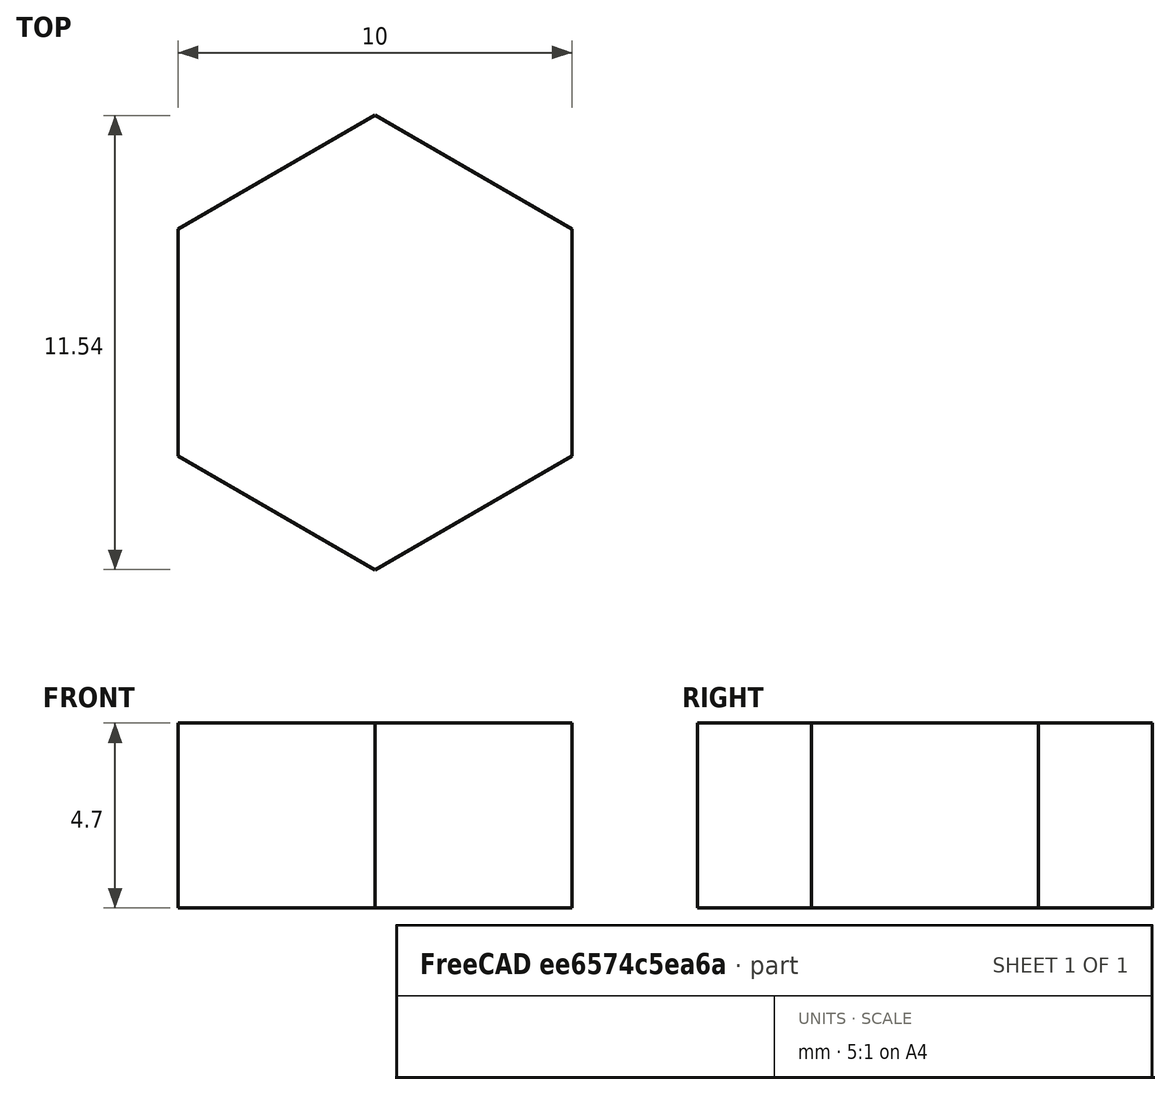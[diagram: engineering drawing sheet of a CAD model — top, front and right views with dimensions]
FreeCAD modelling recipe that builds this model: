
FCSTD DOCUMENT  (FreeCAD 0.16R6700 (Git))
Label: Aula08 - Porca - AUX
License: FreeArt
LicenseURL: http://artlibre.org/licence/lal
objects: Sketcher::SketchObject×2, PartDesign::Pad×1
note: 4 computed .brp shape members not serialized (recipe doc carries the construction recipe); baked Part::Feature solids carry a one-line shape summary decoded from their .brp

FEATURE [Sketcher::SketchObject] Sketch
  sketch-geometry (7):
    g0: LineSegment StartX=5 StartY=2.88675 StartZ=0 EndX=0 EndY=5.7735 EndZ=0
    g1: LineSegment StartX=0 StartY=5.7735 StartZ=0 EndX=-5 EndY=2.88675 EndZ=0
    g2: LineSegment StartX=-5 StartY=2.88675 StartZ=0 EndX=-5 EndY=-2.88675 EndZ=0
    g3: LineSegment StartX=-5 StartY=-2.88675 StartZ=0 EndX=-1e-12 EndY=-5.7735 EndZ=0
    g4: LineSegment StartX=-1e-12 StartY=-5.7735 StartZ=0 EndX=5 EndY=-2.88675 EndZ=0
    g5: LineSegment StartX=5 StartY=-2.88675 StartZ=0 EndX=5 EndY=2.88675 EndZ=0
    g6: Circle [constr] CenterX=0 CenterY=0 CenterZ=0 NormalX=0 NormalY=0 NormalZ=1 Radius=5.7735
  constraints (16):
    c: Coincident(g0,g1)
    c: Coincident(g1,g2)
    c: Coincident(g2,g3)
    c: Coincident(g3,g4)
    c: Coincident(g4,g5)
    c: Coincident(g5,g0)
    c: Equal(g0, g1-g5) x5
    c: PointOnObject(g0,g6)
    c: PointOnObject(g1,g6)
    c: PointOnObject(g2,g6)
    c: PointOnObject(g3,g6)
    c: PointOnObject(g4,g6)
    c: PointOnObject(g5,g6)
    c: Coincident(g6,g-1)
    c: PointOnObject(g0,g-2)
    c: DistanceX(g1,g0) = 10
FEATURE [PartDesign::Pad] Pad
  Length = 4.7
  Length2 = 100
  Sketch = -> Sketch
  Type = 0
FEATURE [Sketcher::SketchObject] Sketch001
  Placement = pos=(0,0,0) rot=(-1,0,0;4.71239rad)
  sketch-geometry (22):
    g0: LineSegment StartX=3 StartY=0 StartZ=0 EndX=1.33699 EndY=0.960141 EndZ=0
    g1: LineSegment StartX=1.33699 StartY=0.960141 StartZ=0 EndX=1.33699 EndY=1.13159 EndZ=0
    g2: LineSegment StartX=1.33699 StartY=1.13159 StartZ=0 EndX=3 EndY=2.09173 EndZ=0
    g3: LineSegment StartX=3 StartY=2.09173 StartZ=0 EndX=1.33699 EndY=3.05187 EndZ=0
    g4: LineSegment StartX=1.33699 StartY=3.05187 StartZ=0 EndX=1.33699 EndY=3.47215 EndZ=0
    g5: LineSegment StartX=1.33699 StartY=3.47215 StartZ=0 EndX=3 EndY=4.43229 EndZ=0
    g6: LineSegment StartX=3 StartY=4.43229 StartZ=0 EndX=1.33699 EndY=5.39243 EndZ=0
    g7: LineSegment StartX=1.33699 StartY=5.39243 StartZ=0 EndX=1.33699 EndY=5.81271 EndZ=0
    g8: LineSegment StartX=1.33699 StartY=5.81271 StartZ=0 EndX=3 EndY=6.77285 EndZ=0
    g9: LineSegment StartX=3 StartY=6.77285 StartZ=0 EndX=1.33699 EndY=7.733 EndZ=0
    g10: LineSegment StartX=1.33699 StartY=7.733 StartZ=0 EndX=1.33699 EndY=7.31271 EndZ=0
    g11: LineSegment StartX=1.33699 StartY=7.31271 StartZ=0 EndX=3 EndY=8.27285 EndZ=0
    g12: LineSegment StartX=3 StartY=8.27285 StartZ=0 EndX=1.33699 EndY=9.233 EndZ=0
    g13: LineSegment StartX=1.33699 StartY=9.233 StartZ=0 EndX=1.33699 EndY=9.40444 EndZ=0
    g14: LineSegment StartX=1.33699 StartY=9.40444 StartZ=0 EndX=3 EndY=10.3646 EndZ=0
    g15: LineSegment StartX=3 StartY=10.3646 StartZ=0 EndX=4.9 EndY=10.3646 EndZ=0
    g16: LineSegment StartX=4.9 StartY=10.3646 StartZ=0 EndX=6 EndY=9.7295 EndZ=0
    g17: LineSegment StartX=6 StartY=9.7295 StartZ=0 EndX=6 EndY=0.635085 EndZ=0
    g18: LineSegment StartX=6 StartY=0.635085 StartZ=0 EndX=4.9 EndY=0 EndZ=0
    g19: LineSegment StartX=4.9 StartY=0 StartZ=0 EndX=3 EndY=0 EndZ=0
    g20: LineSegment [constr] StartX=3 StartY=10.3646 StartZ=0 EndX=3 EndY=0 EndZ=0
    g21: LineSegment [constr] StartX=1.33699 StartY=5.60257 StartZ=0 EndX=3 EndY=5.60257 EndZ=0
  constraints (62):
    c: PointOnObject(g0,g-1)
    c: Coincident(g0,g1)
    c: Coincident(g1,g2)
    c: Coincident(g2,g3)
    c: Coincident(g3,g4)
    c: Vertical(g4)
    c: Coincident(g4,g5)
    c: Coincident(g5,g6)
    c: Coincident(g6,g7)
    c: Vertical(g7)
    c: Coincident(g7,g8)
    c: Coincident(g8,g9)
    c: Coincident(g9,g10)
    c: Vertical(g10)
    c: Coincident(g10,g11)
    c: Coincident(g11,g12)
    c: Coincident(g12,g13)
    c: Vertical(g13)
    c: Coincident(g13,g14)
    c: Coincident(g14,g15)
    c: Horizontal(g15)
    c: Coincident(g15,g16)
    c: Coincident(g16,g17)
    c: Vertical(g17)
    c: Coincident(g17,g18)
    c: PointOnObject(g18,g-1)
    c: Coincident(g18,g19)
    c: Coincident(g19,g0)
    c: Vertical(g1)
    c: PointOnObject(g3,g1)
    c: PointOnObject(g6,g4)
    c: PointOnObject(g9,g7)
    c: PointOnObject(g12,g10)
    c: Equal(g4,g7)
    c: Equal(g7,g10)
    c: Equal(g0,g2)
    c: Equal(g2,g3)
    c: Equal(g3,g5)
    c: Equal(g5,g6)
    c: Equal(g6,g8)
    c: Equal(g8,g9)
    c: Equal(g9,g11)
    c: Equal(g11,g12)
    c: Equal(g12,g14)
    c: Equal(g16,g18)
    c: Equal(g13,g1)
    c: Coincident(g20,g14)
    c: Coincident(g20,g0)
    c: Vertical(g20)
    c: PointOnObject(g11,g20)
    c: PointOnObject(g8,g20)
    c: PointOnObject(g5,g20)
    c: PointOnObject(g2,g20)
    c: Angle(g14,g15) = 2.61799
    c: Angle(g15,g16) = 2.61799
    c: Angle(g18,g19) = 2.61799
    c: PointOnObject(g21,g20)
    c: Horizontal(g21)
    c: Symmetric(g7,g7,g21)
    c: DistanceX(g-1,g14) = 3
    c: DistanceX(g-1,g15) = 4.9
    c: DistanceX(g-1,g16) = 6
